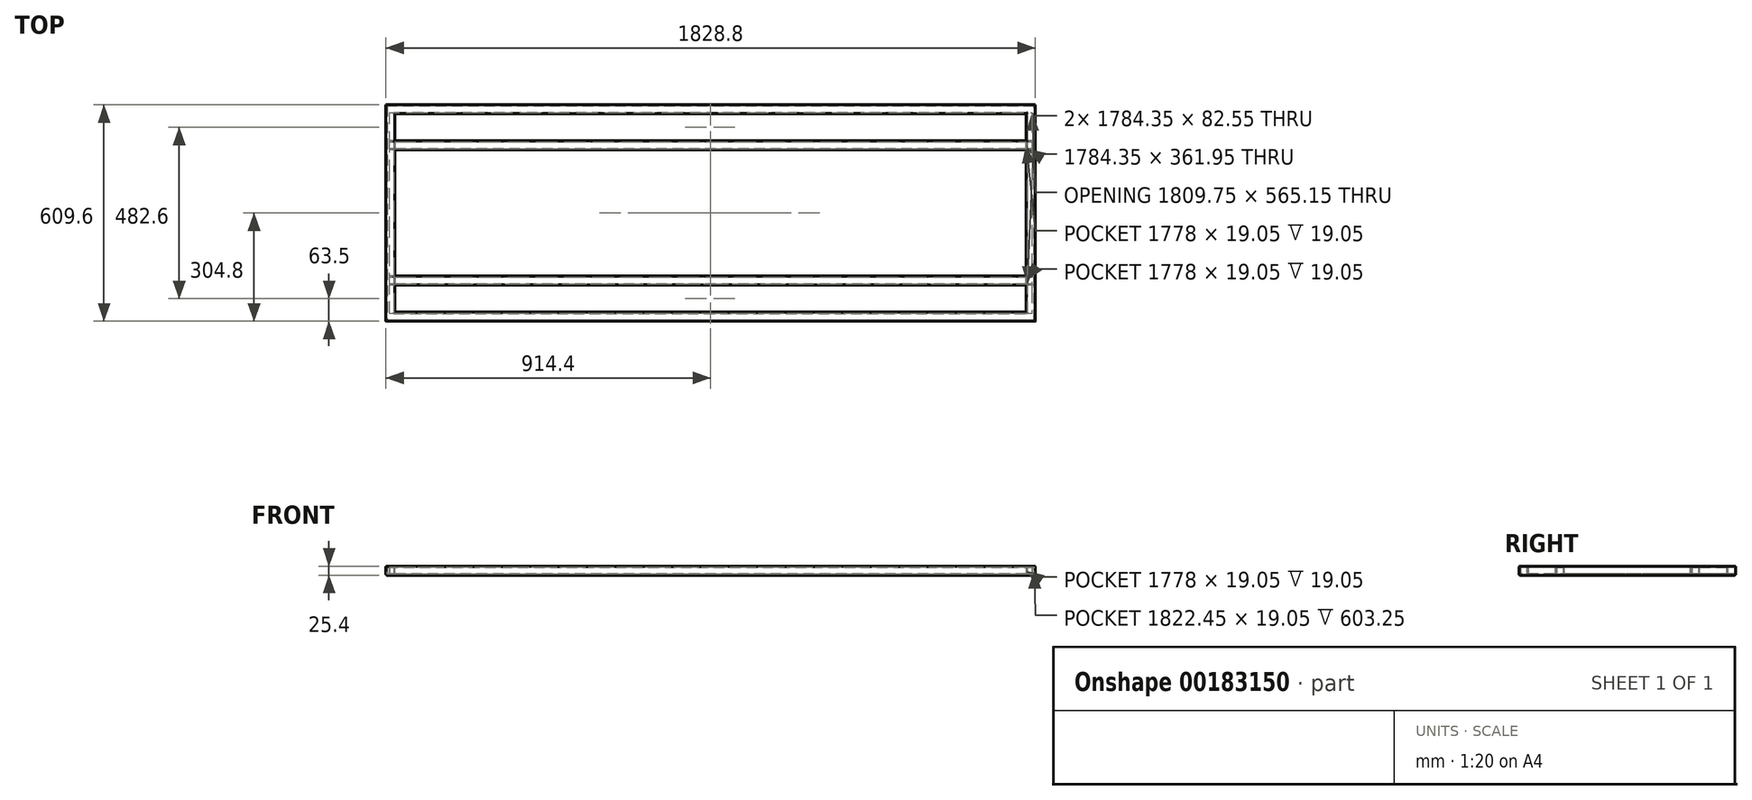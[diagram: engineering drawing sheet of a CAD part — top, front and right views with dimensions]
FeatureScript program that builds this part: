
annotation { "Feature Type Name" : "Feature", "Feature Type Description" : "" }
export const myFeature = defineFeature(function(context is Context, id is Id, definition is map)
    precondition{}
    {
        {
            var Q0;
            Q0=qCreatedBy(makeId("Right.planeOp"),FACE);
            var sketch = newSketch(context, id + "F0", { "sketchPlane" : qUnion([Q0])});
            skLineSegment(sketch, "E0.bottom", {"start": v(-301.63, 12.7) * mm, "end": v(-282.58, 12.7) * mm});
            skLineSegment(sketch, "E0.top", {"start": v(-301.63, -12.7) * mm, "end": v(-282.58, -12.7) * mm});
            skLineSegment(sketch, "E0.left", {"start": v(-304.8, 9.53) * mm, "end": v(-304.8, -9.53) * mm});
            skLineSegment(sketch, "E0.right", {"start": v(-279.4, 9.53) * mm, "end": v(-279.4, -9.53) * mm});
            skPoint(sketch, "E1.visualSharp", {"position": v(-304.8, -12.7) * mm});
            skArc(sketch, "E1.filletArc", {"start": v(-304.8, -9.53) * mm, "mid": v(-303.87, -11.77) * mm, "end": v(-301.63, -12.7) * mm});
            skPoint(sketch, "E2.visualSharp", {"position": v(-279.4, -12.7) * mm});
            skArc(sketch, "E2.filletArc", {"start": v(-282.58, -12.7) * mm, "mid": v(-280.33, -11.77) * mm, "end": v(-279.4, -9.53) * mm});
            skPoint(sketch, "E3.visualSharp", {"position": v(-279.4, 12.7) * mm});
            skArc(sketch, "E3.filletArc", {"start": v(-279.4, 9.53) * mm, "mid": v(-280.33, 11.77) * mm, "end": v(-282.58, 12.7) * mm});
            skPoint(sketch, "E4.visualSharp", {"position": v(-304.8, 12.7) * mm});
            skArc(sketch, "E4.filletArc", {"start": v(-301.63, 12.7) * mm, "mid": v(-303.87, 11.77) * mm, "end": v(-304.8, 9.53) * mm});
            skLineSegment(sketch, "E5.0", {"start": v(-282.58, 9.53) * mm, "end": v(-282.58, 9.53) * mm});
            skLineSegment(sketch, "E5.1", {"start": v(-301.63, 9.53) * mm, "end": v(-282.58, 9.53) * mm});
            skLineSegment(sketch, "E5.2", {"start": v(-282.58, 9.53) * mm, "end": v(-282.58, -9.53) * mm});
            skLineSegment(sketch, "E5.3", {"start": v(-301.63, 9.53) * mm, "end": v(-301.63, 9.53) * mm});
            skLineSegment(sketch, "E5.4", {"start": v(-282.58, -9.53) * mm, "end": v(-282.58, -9.53) * mm});
            skLineSegment(sketch, "E5.5", {"start": v(-301.63, -9.53) * mm, "end": v(-282.58, -9.53) * mm});
            skLineSegment(sketch, "E5.6", {"start": v(-301.63, -9.53) * mm, "end": v(-301.63, -9.53) * mm});
            skLineSegment(sketch, "E5.7", {"start": v(-301.63, 9.53) * mm, "end": v(-301.63, -9.53) * mm});
            skPoint(sketch, "E6", {"position": v(-279.4, 0) * mm});
            skSolve(sketch);
        }
        {
            var Q0;
            Q0=qCreatedBy(makeId("Top.planeOp"),FACE);
            var sketch = newSketch(context, id + "F1", { "sketchPlane" : qUnion([Q0])});
            skLineSegment(sketch, "E7.bottom", {"start": v(914.4, -304.8) * mm, "end": v(-914.4, -304.8) * mm});
            skLineSegment(sketch, "E7.top", {"start": v(914.4, 304.8) * mm, "end": v(-914.4, 304.8) * mm});
            skLineSegment(sketch, "E7.left", {"start": v(914.4, -304.8) * mm, "end": v(914.4, 304.8) * mm});
            skLineSegment(sketch, "E7.right", {"start": v(-914.4, -304.8) * mm, "end": v(-914.4, 304.8) * mm});
            skPoint(sketch, "E7.middle", {"position": v(0, 0) * mm});
            skSolve(sketch);
        }
        {
            var Q0;
            Q0=makeQuery(id+"F0.imprint","IMPRINT",FACE,{"disambiguationData":[TD([[makeQuery(id+"F0.imprint","IMPRINT",EDGE,{"derivedFrom":sQuery(id+"F0.wireOp",EDGE,"E0.bottom")}),-1.0]])]});
            var Q1;
            Q1=sQuery(id+"F1.wireOp",EDGE,"E7.bottom");
            var Q2;
            Q2=sQuery(id+"F1.wireOp",EDGE,"E7.right");
            var Q3;
            Q3=sQuery(id+"F1.wireOp",EDGE,"E7.top");
            var Q4;
            Q4=sQuery(id+"F1.wireOp",EDGE,"E7.left");
            sweep(context, id + "F2", {"profiles" : qUnion([Q0]), "path" : qUnion([Q1, Q2, Q3, Q4])});
        }
        {
            var Q0;
            Q0=qCreatedBy(makeId("Right.planeOp"),FACE);
            var sketch = newSketch(context, id + "F3", { "sketchPlane" : qUnion([Q0])});
            skLineSegment(sketch, "E8.bottom", {"start": v(-200.03, 12.7) * mm, "end": v(-180.98, 12.7) * mm});
            skLineSegment(sketch, "E8.top", {"start": v(-200.03, -12.7) * mm, "end": v(-180.98, -12.7) * mm});
            skLineSegment(sketch, "E8.left", {"start": v(-203.2, 9.53) * mm, "end": v(-203.2, -9.53) * mm});
            skLineSegment(sketch, "E8.right", {"start": v(-177.8, 9.53) * mm, "end": v(-177.8, -9.53) * mm});
            skPoint(sketch, "E9.visualSharp", {"position": v(-203.2, -12.7) * mm});
            skArc(sketch, "E9.filletArc", {"start": v(-203.2, -9.53) * mm, "mid": v(-202.27, -11.77) * mm, "end": v(-200.03, -12.7) * mm});
            skPoint(sketch, "E10.visualSharp", {"position": v(-177.8, -12.7) * mm});
            skArc(sketch, "E10.filletArc", {"start": v(-180.98, -12.7) * mm, "mid": v(-178.73, -11.77) * mm, "end": v(-177.8, -9.52) * mm});
            skPoint(sketch, "E11.visualSharp", {"position": v(-177.8, 12.7) * mm});
            skArc(sketch, "E11.filletArc", {"start": v(-177.8, 9.53) * mm, "mid": v(-178.73, 11.77) * mm, "end": v(-180.98, 12.7) * mm});
            skPoint(sketch, "E12.visualSharp", {"position": v(-203.2, 12.7) * mm});
            skArc(sketch, "E12.filletArc", {"start": v(-200.03, 12.7) * mm, "mid": v(-202.27, 11.77) * mm, "end": v(-203.2, 9.53) * mm});
            skLineSegment(sketch, "E13.0", {"start": v(-180.98, 9.53) * mm, "end": v(-180.98, 9.53) * mm});
            skLineSegment(sketch, "E13.1", {"start": v(-200.03, 9.52) * mm, "end": v(-180.98, 9.52) * mm});
            skLineSegment(sketch, "E13.2", {"start": v(-180.98, 9.53) * mm, "end": v(-180.98, -9.53) * mm});
            skLineSegment(sketch, "E13.3", {"start": v(-200.03, 9.53) * mm, "end": v(-200.03, 9.53) * mm});
            skLineSegment(sketch, "E13.4", {"start": v(-180.98, -9.52) * mm, "end": v(-180.98, -9.52) * mm});
            skLineSegment(sketch, "E13.5", {"start": v(-200.03, -9.52) * mm, "end": v(-180.98, -9.52) * mm});
            skLineSegment(sketch, "E13.6", {"start": v(-200.03, -9.53) * mm, "end": v(-200.03, -9.53) * mm});
            skLineSegment(sketch, "E13.7", {"start": v(-200.03, 9.53) * mm, "end": v(-200.03, -9.53) * mm});
            skPoint(sketch, "E14", {"position": v(-177.8, 0) * mm});
            skArc(sketch, "E15.MirrorCS", {"start": v(203.2, -9.53) * mm, "mid": v(202.27, -11.77) * mm, "end": v(200.03, -12.7) * mm});
            skArc(sketch, "E16.MirrorCS", {"start": v(180.98, -12.7) * mm, "mid": v(178.73, -11.77) * mm, "end": v(177.8, -9.52) * mm});
            skArc(sketch, "E17.MirrorCS", {"start": v(177.8, 9.53) * mm, "mid": v(178.73, 11.77) * mm, "end": v(180.98, 12.7) * mm});
            skArc(sketch, "E18.MirrorCS", {"start": v(200.03, 12.7) * mm, "mid": v(202.27, 11.77) * mm, "end": v(203.2, 9.53) * mm});
            skLineSegment(sketch, "E19.MirrorCS", {"start": v(177.8, 9.53) * mm, "end": v(177.8, -9.53) * mm});
            skLineSegment(sketch, "E20.MirrorCS", {"start": v(180.98, 9.53) * mm, "end": v(180.98, -9.53) * mm});
            skLineSegment(sketch, "E21.MirrorCS", {"start": v(200.03, 12.7) * mm, "end": v(180.98, 12.7) * mm});
            skLineSegment(sketch, "E22.MirrorCS", {"start": v(200.03, -12.7) * mm, "end": v(180.98, -12.7) * mm});
            skLineSegment(sketch, "E23.MirrorCS", {"start": v(200.03, 9.52) * mm, "end": v(180.98, 9.52) * mm});
            skLineSegment(sketch, "E24.MirrorCS", {"start": v(200.03, -9.52) * mm, "end": v(180.98, -9.52) * mm});
            skPoint(sketch, "E25.MirrorP", {"position": v(177.8, 0) * mm});
            skPoint(sketch, "E26.MirrorP", {"position": v(203.2, 12.7) * mm});
            skLineSegment(sketch, "E27.MirrorCS", {"start": v(180.98, 9.53) * mm, "end": v(180.98, 9.53) * mm});
            skPoint(sketch, "E28.MirrorP", {"position": v(177.8, 12.7) * mm});
            skLineSegment(sketch, "E29.MirrorCS", {"start": v(200.03, -9.53) * mm, "end": v(200.03, -9.53) * mm});
            skPoint(sketch, "E30.MirrorP", {"position": v(203.2, -12.7) * mm});
            skLineSegment(sketch, "E31.MirrorCS", {"start": v(200.03, 9.53) * mm, "end": v(200.03, 9.53) * mm});
            skLineSegment(sketch, "E32.MirrorCS", {"start": v(203.2, 9.53) * mm, "end": v(203.2, -9.53) * mm});
            skLineSegment(sketch, "E33.MirrorCS", {"start": v(200.03, 9.53) * mm, "end": v(200.03, -9.53) * mm});
            skPoint(sketch, "E34.MirrorP", {"position": v(177.8, -12.7) * mm});
            skLineSegment(sketch, "E35.MirrorCS", {"start": v(180.98, -9.52) * mm, "end": v(180.98, -9.52) * mm});
            skSolve(sketch);
        }
        {
            var Q0;
            Q0 = qSketchRegion(id + "F3", true);
            extrude(context, id + "F4", {"entities" : qUnion([Q0]), "operationType" : NewBodyOperationType.ADD, "endBound" : BoundingType.SYMMETRIC, "depth" : 1809.75 * mm});
        }
    });
